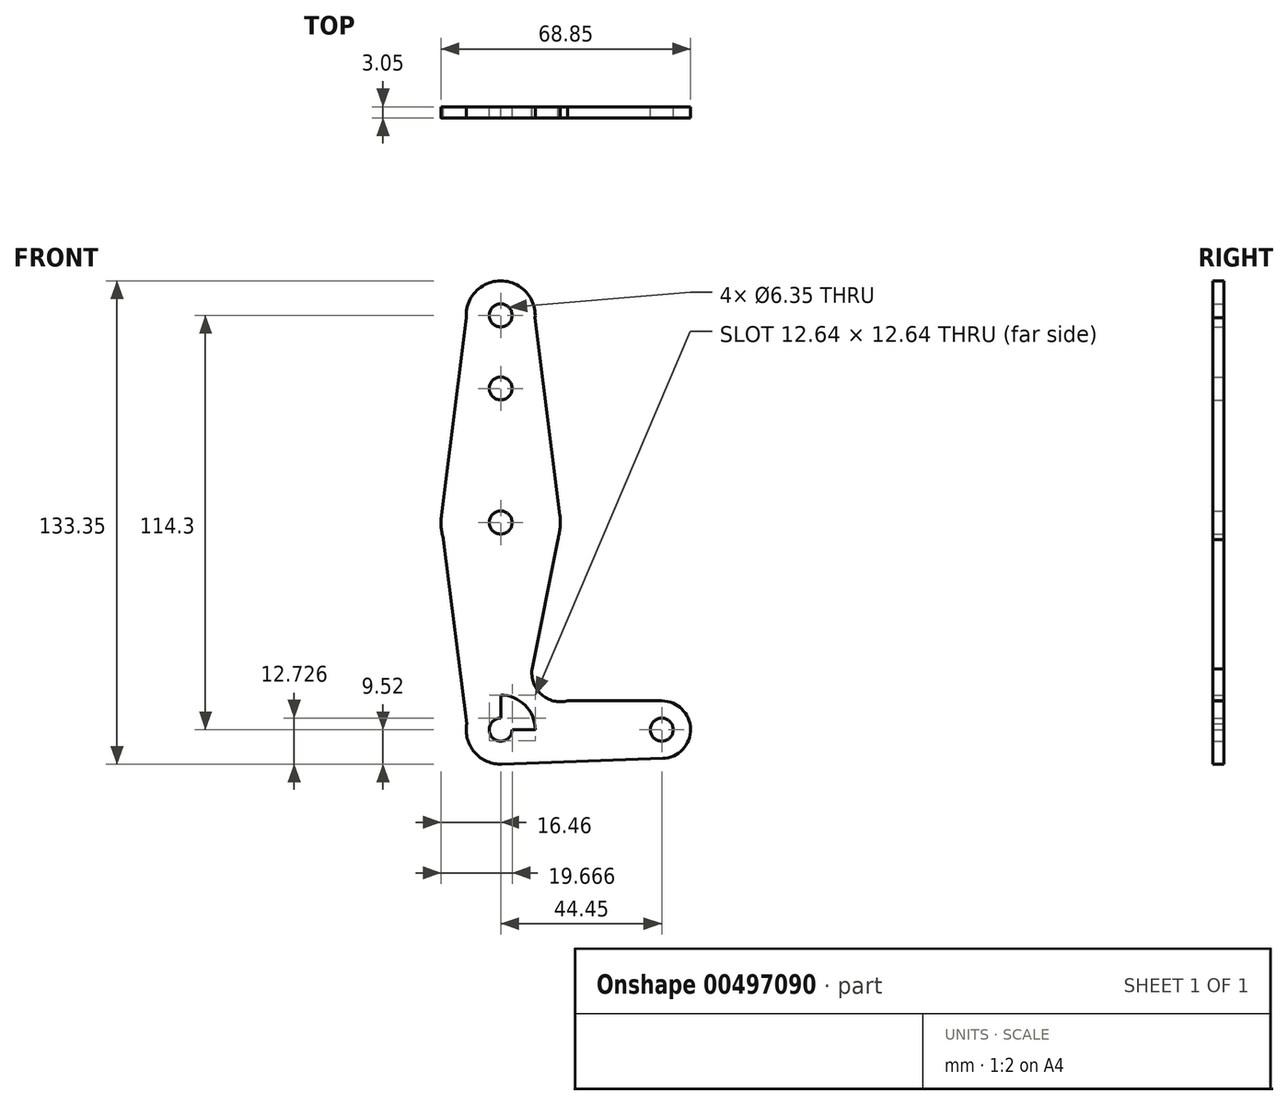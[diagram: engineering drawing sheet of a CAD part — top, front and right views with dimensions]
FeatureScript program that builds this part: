
annotation { "Feature Type Name" : "Feature", "Feature Type Description" : "" }
export const myFeature = defineFeature(function(context is Context, id is Id, definition is map)
    precondition{}
    {
        {
            var Q0;
            Q0=qCreatedBy(makeId("Front.planeOp"),FACE);
            var sketch = newSketch(context, id + "F0", { "sketchPlane" : qUnion([Q0])});
            skLineSegment(sketch, "E0", {"start": v(0, 114.3) * mm, "end": v(0, 0) * mm});
            skLineSegment(sketch, "E1", {"start": v(0, 0) * mm, "end": v(44.45, 0) * mm});
            skCircle(sketch, "E2", {"center": v(0, 0) * mm, "radius": 9.53 * mm});
            skCircle(sketch, "E3", {"center": v(0, 57.15) * mm, "radius": 16.46 * mm});
            skCircle(sketch, "E4", {"center": v(0, 114.3) * mm, "radius": 9.53 * mm});
            skCircle(sketch, "E5", {"center": v(44.45, 0) * mm, "radius": 7.94 * mm});
            skLineSegment(sketch, "E6", {"start": v(9.04, 117.3) * mm, "end": v(16.33, 59.2) * mm});
            skLineSegment(sketch, "E7", {"start": v(16.33, 59.2) * mm, "end": v(15.76, 52.41) * mm});
            skLineSegment(sketch, "E8", {"start": v(44.73, -7.93) * mm, "end": v(0, -9.53) * mm});
            skCircle(sketch, "E9", {"center": v(0, 94.16) * mm, "radius": 1.59 * mm});
            skCircle(sketch, "E10", {"center": v(0, 57.15) * mm, "radius": 3.18 * mm});
            skCircle(sketch, "E11", {"center": v(0, 0) * mm, "radius": 3.18 * mm});
            skCircle(sketch, "E12", {"center": v(44.45, 0) * mm, "radius": 3.18 * mm});
            skCircle(sketch, "E13", {"center": v(0, 114.3) * mm, "radius": 3.18 * mm});
            skCircle(sketch, "E14", {"center": v(0, 94.16) * mm, "radius": 3.18 * mm});
            skLineSegment(sketch, "E15", {"start": v(-15.76, 52.41) * mm, "end": v(-9.19, 0) * mm});
            skLineSegment(sketch, "E16", {"start": v(-9.04, 117.3) * mm, "end": v(-16.33, 59.2) * mm});
            skArc(sketch, "E17", {"start": v(23.66, 19.19) * mm, "mid": v(17.81, 7.8) * mm, "end": v(8.68, 16.78) * mm});
            skLineSegment(sketch, "E18", {"start": v(15.76, 52.41) * mm, "end": v(8.68, 16.78) * mm});
            skLineSegment(sketch, "E19", {"start": v(44.45, 7.94) * mm, "end": v(18.52, 7.94) * mm});
            skSolve(sketch);
        }
        {
            var Q0;
            Q0 = qSketchRegion(id + "F0", true);
            extrude(context, id + "F1", {"entities" : qUnion([Q0]), "depth" : 3.05 * mm});
        }
    });
